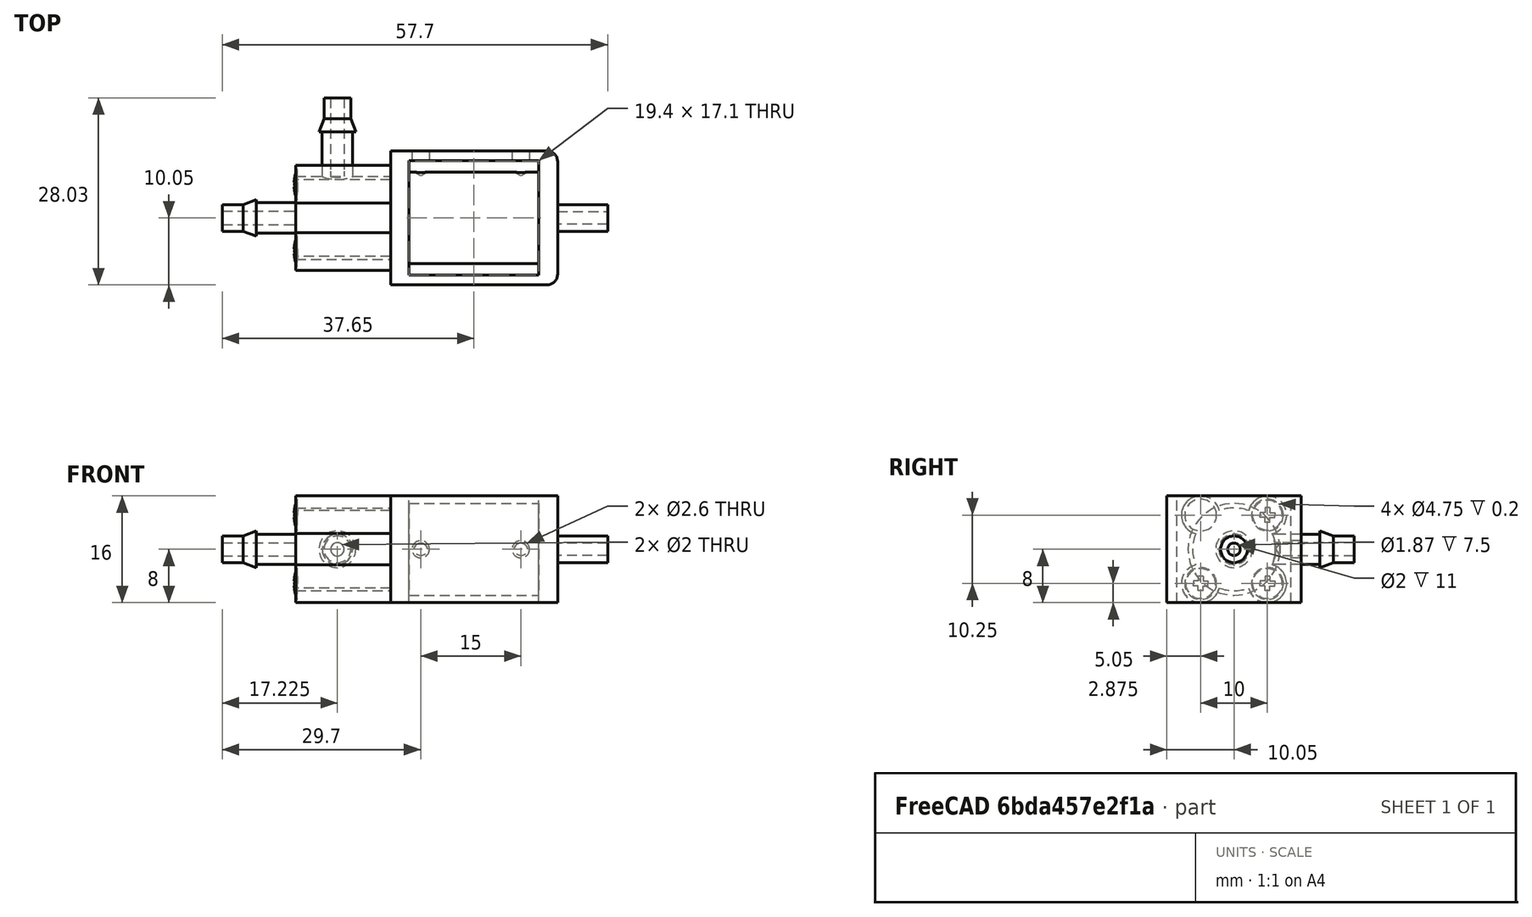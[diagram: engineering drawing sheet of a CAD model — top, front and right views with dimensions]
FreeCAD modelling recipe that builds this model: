
FCSTD DOCUMENT  (FreeCAD 0.19R)
Label: OTS-0004_three-way-valve
License: All rights reserved
LicenseURL: http://en.wikipedia.org/wiki/All_rights_reserved
objects: Sketcher::SketchObject×10, PartDesign::Plane×8, PartDesign::Pad×5, PartDesign::Line×3, PartDesign::Revolution×2, PartDesign::Hole×2, PartDesign::PolarPattern×2, PartDesign::LinearPattern×2, PartDesign::Body×1, PartDesign::FeatureBase×1, PartDesign::Pocket×1
note: 47 computed .brp shape members not serialized (recipe doc carries the construction recipe); baked Part::Feature solids carry a one-line shape summary decoded from their .brp

FEATURE [Sketcher::SketchObject] Sketch
  FullyConstrained = true
  MapMode = 5
  Support = -> [XY_Plane]
  sketch-geometry (14):
    g0: LineSegment StartX=0 StartY=0 StartZ=0 EndX=23.4 EndY=0 EndZ=0
    g1: LineSegment StartX=25 StartY=1.6 StartZ=0 EndX=25 EndY=18.5 EndZ=0
    g2: LineSegment StartX=23.4 StartY=20.1 StartZ=0 EndX=0 EndY=20.1 EndZ=0
    g3: LineSegment StartX=0 StartY=20.1 StartZ=0 EndX=0 EndY=0 EndZ=0
    g4: ArcOfCircle CenterX=23.4 CenterY=18.5 CenterZ=0 NormalX=0 NormalY=0 NormalZ=1 AngleXU=0 Radius=1.6 StartAngle=-9e-16 EndAngle=1.5708
    g5: GeomPoint X=25 Y=20.1 Z=0
    g6: ArcOfCircle CenterX=23.4 CenterY=1.6 CenterZ=0 NormalX=0 NormalY=0 NormalZ=1 AngleXU=0 Radius=1.6 StartAngle=4.71239 EndAngle=6.28319
    g7: GeomPoint X=25 Y=0 Z=0
    g8: LineSegment StartX=2.75 StartY=18.6 StartZ=0 EndX=22.15 EndY=18.6 EndZ=0
    g9: LineSegment StartX=2.75 StartY=18.6 StartZ=0 EndX=2.75 EndY=1.5 EndZ=0
    g10: LineSegment StartX=2.75 StartY=1.5 StartZ=0 EndX=22.15 EndY=1.5 EndZ=0
    g11: GeomPoint X=0 Y=10.05 Z=0
    g12: LineSegment StartX=0 StartY=10.05 StartZ=0 EndX=25 EndY=10.05 EndZ=0
    g13: LineSegment StartX=22.15 StartY=18.6 StartZ=0 EndX=22.15 EndY=1.5 EndZ=0
  constraints (34):
    c: Coincident(g2,g3)
    c: Coincident(g3,g0)
    c: Horizontal(g0)
    c: Horizontal(g2)
    c: Vertical(g1)
    c: Vertical(g3)
    c: Coincident(g0,g-1)
    c: Distance(g0,g7) = 25
    c: Distance(g3) = 20.1
    c: PointOnObject(g5,g1)
    c: PointOnObject(g5,g2)
    c: Tangent(g1,g4) = -1.5708
    c: Tangent(g2,g4) = -1.5708
    c: PointOnObject(g7,g0)
    c: PointOnObject(g7,g1)
    c: Tangent(g0,g6) = -1.5708
    c: Tangent(g1,g6) = -1.5708
    c: Equal(g6,g4)
    c: Diameter(g4) = 3.2
    c: Horizontal(g8)
    c: Coincident(g9,g8)
    c: Vertical(g9)
    c: Coincident(g10,g9)
    c: Horizontal(g10)
    c: Symmetric(g3,g3,g11)
    c: Coincident(g12,g11)
    c: PointOnObject(g12,g1)
    c: Symmetric(g9,g8,g12)
    c: Distance(g9,g3) = 2.75
    c: Coincident(g13,g8)
    c: Coincident(g13,g10)
    c: Vertical(g13)
    c: Distance(g12,g13) = 2.85
    c: Distance(g2,g8) = 1.5
FEATURE [PartDesign::Body] Body  label="3-Way Solenoid Valve"
  BaseFeature = -> DatumPlane001
  Group = -> [BaseFeature,Sketch,Pad,DatumPlane,Sketch001,Pad001,Sketch002,Pad002,Sketch003,Pad003,DatumLine,DatumPlane002,Sketch005,Revolution,DatumPlane003,Sketch007,DatumLine001,PolarPattern,DatumPlane005,Sketch009,Hole001,DatumLine002,DatumPlane006,Sketch010,Revolution001,DatumPlane007,Sketch011,Pocket,LinearPattern,LinearPattern001,Pad004,PolarPattern001,Hole,DatumPlane004,Sketch008]
  Origin = -> Origin
  Tip = -> Pad004
FEATURE [PartDesign::Pad] Pad
  BaseFeature = -> BaseFeature
  Direction = (1,1,1)
  Length = 16
  Length2 = 100
  Midplane = true
  Profile = -> Sketch
  Type = 0
FEATURE [PartDesign::Plane] DatumPlane
  Length = 63.3231
  MapMode = 5
  Placement = pos=(22.15,0,0) rot=(0.57735,-0.57735,-0.57735;2.0944rad)
  ResizeMode = 0
  Support = -> [Pad]
  Width = 60.2981
FEATURE [Sketcher::SketchObject] Sketch001
  ExternalGeometry = -> [Pad]
  FullyConstrained = true
  MapMode = 5
  Placement = pos=(22.15,0,0) rot=(0.57735,-0.57735,-0.57735;2.0944rad)
  Support = -> [DatumPlane]
  sketch-geometry (2):
    g0: Circle CenterX=-10.05 CenterY=-1e-16 CenterZ=0 NormalX=0 NormalY=0 NormalZ=1 AngleXU=0 Radius=6.875
    g1: LineSegment StartX=-18.6 StartY=8 StartZ=0 EndX=-1.5 EndY=-8 EndZ=0
  constraints (4):
    c: Coincident(g1,g-6)
    c: Coincident(g1,g-5)
    c: Symmetric(g1,g1,g0)
    c: Radius(g0) = 6.875
FEATURE [PartDesign::Pad] Pad001
  BaseFeature = -> Pad
  Direction = (1,1,1)
  Length = 10
  Length2 = 100
  Profile = -> Sketch001
  Type = 2
FEATURE [PartDesign::Plane] DatumPlane001
  Length = 63.3231
  MapMode = 5
  Placement = pos=(0,0,0) rot=(0.57735,-0.57735,-0.57735;2.0944rad)
  ResizeMode = 0
  Support = -> [Pad001]
  Width = 60.2981
FEATURE [PartDesign::FeatureBase] BaseFeature
  BaseFeature = -> DatumPlane001
FEATURE [Sketcher::SketchObject] Sketch002
  ExternalGeometry = -> [Pad001]
  FullyConstrained = false
  MapMode = 5
  Placement = pos=(0,0,0) rot=(0.57735,-0.57735,-0.57735;2.0944rad)
  Support = -> [DatumPlane001]
  sketch-geometry (15):
    g0: GeomPoint X=-10.05 Y=1e-16 Z=0
    g1: LineSegment StartX=0 StartY=8 StartZ=0 EndX=-20.1 EndY=-8 EndZ=0
    g2: ArcOfCircle CenterX=-10.05 CenterY=1e-16 CenterZ=0 NormalX=0 NormalY=0 NormalZ=1 AngleXU=0 Radius=6.2 StartAngle=2.75344 EndAngle=3.52974
    g3: ArcOfCircle CenterX=-15.05 CenterY=5.125 CenterZ=0 NormalX=0 NormalY=0 NormalZ=1 AngleXU=0 Radius=2.875 StartAngle=0.235196 EndAngle=4.4525
    g4: ArcOfCircle CenterX=-5.05 CenterY=5.125 CenterZ=0 NormalX=0 NormalY=0 NormalZ=1 AngleXU=0 Radius=2.875 StartAngle=4.97228 EndAngle=9.18958
    g5: LineSegment StartX=-10.05 StartY=1e-16 StartZ=0 EndX=-10.05 EndY=8 EndZ=0
    g6: Circle CenterX=-15.05 CenterY=5.125 CenterZ=0 NormalX=0 NormalY=0 NormalZ=1 AngleXU=0 Radius=2.375
    g7: Circle CenterX=-5.05 CenterY=5.125 CenterZ=0 NormalX=0 NormalY=0 NormalZ=1 AngleXU=0 Radius=2.375
    g8: ArcOfCircle CenterX=-10.05 CenterY=1e-16 CenterZ=0 NormalX=0 NormalY=0 NormalZ=1 AngleXU=0 Radius=6.2 StartAngle=1.20734 EndAngle=1.93425
    g9: ArcOfCircle CenterX=-15.05 CenterY=-5.125 CenterZ=0 NormalX=0 NormalY=0 NormalZ=1 AngleXU=0 Radius=2.875 StartAngle=1.83068 EndAngle=6.04799
    g10: Circle CenterX=-15.05 CenterY=-5.125 CenterZ=0 NormalX=0 NormalY=0 NormalZ=1 AngleXU=0 Radius=2.375
    g11: ArcOfCircle CenterX=-5.05 CenterY=-5.125 CenterZ=0 NormalX=0 NormalY=0 NormalZ=1 AngleXU=0 Radius=2.875 StartAngle=3.37679 EndAngle=7.5941
    g12: Circle CenterX=-5.05 CenterY=-5.125 CenterZ=0 NormalX=0 NormalY=0 NormalZ=1 AngleXU=0 Radius=2.375
    g13: ArcOfCircle CenterX=-10.05 CenterY=1e-16 CenterZ=0 NormalX=0 NormalY=0 NormalZ=1 AngleXU=0 Radius=6.2 StartAngle=4.34893 EndAngle=5.07585
    g14: ArcOfCircle CenterX=-10.05 CenterY=1e-16 CenterZ=0 NormalX=0 NormalY=0 NormalZ=1 AngleXU=0 Radius=6.2 StartAngle=5.89504 EndAngle=6.67133
  constraints (38):
    c: Coincident(g1,g-5)
    c: Coincident(g1,g-4)
    c: Symmetric(g1,g1,g0)
    c: Coincident(g2,g0)
    c: Radius(g2) = 6.2
    c: Tangent(g3,g-5)
    c: Tangent(g4,g-5)
    c: Equal(g3,g4)
    c: Diameter(g3) = 5.75
    c: Distance(g3,g4) = 10
    c: Coincident(g5,g2)
    c: PointOnObject(g5,g-5)
    c: Symmetric(g4,g3,g5)
    c: Coincident(g6,g3)
    c: Coincident(g7,g4)
    c: Equal(g7,g6)
    c: Diameter(g6) = 4.75
    c: Equal(g2,g8)
    c: Coincident(g2,g8)
    c: Coincident(g3,g8)
    c: Coincident(g3,g2)
    c: Coincident(g4,g8)
    c: Coincident(g4,g14)
    c: Equal(g9,g11)
    c: Diameter(g9) = 5.75
    c: Distance(g9,g11) = 10
    c: Coincident(g10,g9)
    c: Coincident(g12,g11)
    c: Equal(g12,g10)
    c: Diameter(g10) = 4.75
    c: Equal(g2,g13)
    c: PointOnObject(g2,g9)
    c: Coincident(g2,g13)
    c: PointOnObject(g13,g9)
    c: Equal(g13,g14)
    c: PointOnObject(g13,g11)
    c: Coincident(g13,g14)
    c: PointOnObject(g14,g11)
FEATURE [PartDesign::Pad] Pad002
  BaseFeature = -> Pad001
  Direction = (1,1,1)
  Length = 14.2
  Length2 = 100
  Profile = -> Sketch002
  Type = 0
FEATURE [Sketcher::SketchObject] Sketch003
  ExternalGeometry = -> [Pad001]
  FullyConstrained = false
  MapMode = 5
  Placement = pos=(0,0,0) rot=(0.57735,-0.57735,-0.57735;2.0944rad)
  Support = -> [DatumPlane001]
  expr: Constraints[25] = Sketch002.Constraints[25]
  expr: Constraints[24] = Sketch002.Constraints[24]
  expr: Constraints[9] = Sketch002.Constraints[9]
  expr: Constraints[16] = Sketch002.Constraints[16]
  expr: Constraints[8] = Sketch002.Constraints[8]
  expr: Constraints[29] = Sketch002.Constraints[29]
  expr: Constraints[4] = Sketch002.Constraints[4]
  sketch-geometry (15):
    g0: GeomPoint X=-10.05 Y=1e-16 Z=0
    g1: LineSegment StartX=0 StartY=8 StartZ=0 EndX=-20.1 EndY=-8 EndZ=0
    g2: ArcOfCircle CenterX=-10.05 CenterY=1e-16 CenterZ=0 NormalX=0 NormalY=0 NormalZ=1 AngleXU=0 Radius=6.2 StartAngle=2.75344 EndAngle=3.52974
    g3: ArcOfCircle CenterX=-15.05 CenterY=5.125 CenterZ=0 NormalX=0 NormalY=0 NormalZ=1 AngleXU=0 Radius=2.875 StartAngle=0.235196 EndAngle=4.4525
    g4: ArcOfCircle CenterX=-5.05 CenterY=5.125 CenterZ=0 NormalX=0 NormalY=0 NormalZ=1 AngleXU=0 Radius=2.875 StartAngle=4.97228 EndAngle=9.18958
    g5: LineSegment StartX=-10.05 StartY=1e-16 StartZ=0 EndX=-10.05 EndY=8 EndZ=0
    g6: Circle CenterX=-15.05 CenterY=5.125 CenterZ=0 NormalX=0 NormalY=0 NormalZ=1 AngleXU=0 Radius=2.375
    g7: Circle CenterX=-5.05 CenterY=5.125 CenterZ=0 NormalX=0 NormalY=0 NormalZ=1 AngleXU=0 Radius=2.375
    g8: ArcOfCircle CenterX=-10.05 CenterY=1e-16 CenterZ=0 NormalX=0 NormalY=0 NormalZ=1 AngleXU=0 Radius=6.2 StartAngle=1.20734 EndAngle=1.93425
    g9: ArcOfCircle CenterX=-15.05 CenterY=-5.125 CenterZ=0 NormalX=0 NormalY=0 NormalZ=1 AngleXU=0 Radius=2.875 StartAngle=1.83068 EndAngle=6.04799
    g10: Circle CenterX=-15.05 CenterY=-5.125 CenterZ=0 NormalX=0 NormalY=0 NormalZ=1 AngleXU=0 Radius=2.375
    g11: ArcOfCircle CenterX=-5.05 CenterY=-5.125 CenterZ=0 NormalX=0 NormalY=0 NormalZ=1 AngleXU=0 Radius=2.875 StartAngle=3.37679 EndAngle=7.5941
    g12: Circle CenterX=-5.05 CenterY=-5.125 CenterZ=0 NormalX=0 NormalY=0 NormalZ=1 AngleXU=0 Radius=2.375
    g13: ArcOfCircle CenterX=-10.05 CenterY=1e-16 CenterZ=0 NormalX=0 NormalY=0 NormalZ=1 AngleXU=0 Radius=6.2 StartAngle=4.34893 EndAngle=5.07585
    g14: ArcOfCircle CenterX=-10.05 CenterY=1e-16 CenterZ=0 NormalX=0 NormalY=0 NormalZ=1 AngleXU=0 Radius=6.2 StartAngle=5.89504 EndAngle=6.67133
  constraints (38):
    c: Coincident(g1,g-5)
    c: Coincident(g1,g-4)
    c: Symmetric(g1,g1,g0)
    c: Coincident(g2,g0)
    c: Radius(g2) = 6.2
    c: Tangent(g3,g-5)
    c: Tangent(g4,g-5)
    c: Equal(g3,g4)
    c: Diameter(g3) = 5.75
    c: Distance(g3,g4) = 10
    c: Coincident(g5,g2)
    c: PointOnObject(g5,g-5)
    c: Symmetric(g4,g3,g5)
    c: Coincident(g6,g3)
    c: Coincident(g7,g4)
    c: Equal(g7,g6)
    c: Diameter(g6) = 4.75
    c: Equal(g2,g8)
    c: Coincident(g2,g8)
    c: Coincident(g3,g8)
    c: Coincident(g3,g2)
    c: Coincident(g4,g8)
    c: Coincident(g4,g14)
    c: Equal(g9,g11)
    c: Diameter(g9) = 5.75
    c: Distance(g9,g11) = 10
    c: Coincident(g10,g9)
    c: Coincident(g12,g11)
    c: Equal(g12,g10)
    c: Diameter(g10) = 4.75
    c: Equal(g2,g13)
    c: PointOnObject(g2,g9)
    c: Coincident(g2,g13)
    c: PointOnObject(g13,g9)
    c: Equal(g13,g14)
    c: PointOnObject(g13,g11)
    c: Coincident(g13,g14)
    c: PointOnObject(g14,g11)
FEATURE [PartDesign::Pad] Pad003
  BaseFeature = -> Pad002
  Direction = (1,1,1)
  Length = 14
  Length2 = 100
  Profile = -> Sketch003
  Type = 0
FEATURE [PartDesign::Line] DatumLine
  AttacherType = Attacher::AttachEngineLine
  Length = 20
  MapMode = 42
  Placement = pos=(0,10.05,5.9e-15) rot=(0.57735,0.57735,0.57735;2.0944rad)
  ResizeMode = 0
  Support = -> [Pad003]
FEATURE [PartDesign::Plane] DatumPlane002
  Length = 64.0876
  MapMode = 3
  Placement = pos=(0,10.05,5.9e-15) rot=(0.707107,0.707107,0;3.14159rad)
  ResizeMode = 0
  Support = -> [DatumLine]
  Width = 68.7626
FEATURE [Sketcher::SketchObject] Sketch005
  FullyConstrained = false
  MapMode = 5
  Placement = pos=(0,10.05,-5e-15) rot=(0.707107,0.707107,0;3.14159rad)
  Support = -> [DatumPlane002]
  sketch-geometry (12):
    g0: LineSegment StartX=0 StartY=-14.2 StartZ=0 EndX=0 EndY=-25.2 EndZ=0
    g1: LineSegment StartX=-2.75 StartY=-20.1 StartZ=0 EndX=-2 EndY=-22.1 EndZ=0
    g2: LineSegment StartX=-2 StartY=-22.1 StartZ=0 EndX=-2 EndY=-25.2 EndZ=0
    g3: LineSegment StartX=-2.75 StartY=-20.1 StartZ=0 EndX=-2.275 EndY=-20.1 EndZ=0
    g4: LineSegment StartX=-2.275 StartY=-20.1 StartZ=0 EndX=-2.275 EndY=-14.2 EndZ=0
    g5: LineSegment StartX=-2.275 StartY=-14.2 StartZ=0 EndX=-1 EndY=-14.1999 EndZ=0
    g6: LineSegment StartX=-2 StartY=-25.2 StartZ=0 EndX=0 EndY=-25.2 EndZ=0
    g7: LineSegment StartX=-2 StartY=-25.2 StartZ=0 EndX=-1 EndY=-25.2 EndZ=0
    g8: LineSegment StartX=-1 StartY=-25.2 StartZ=0 EndX=-1 EndY=-14.1999 EndZ=0
    g9: LineSegment StartX=-2.275 StartY=-14.2 StartZ=0 EndX=-2.275 EndY=-10.8366 EndZ=0
    g10: LineSegment StartX=-2.275 StartY=-10.8366 StartZ=0 EndX=-1 EndY=-10.8366 EndZ=0
    g11: LineSegment StartX=-1 StartY=-14.1999 StartZ=0 EndX=-1 EndY=-10.8366 EndZ=0
  constraints (33):
    c: PointOnObject(g0,g-2)
    c: PointOnObject(g0,g-2)
    c: DistanceY(g-1,g0) = -14.2
    c: Coincident(g2,g1)
    c: Vertical(g2)
    c: Coincident(g3,g1)
    c: Horizontal(g3)
    c: Coincident(g4,g3)
    c: Vertical(g4)
    c: Horizontal(g0,g4)
    c: Coincident(g5,g4)
    c: Coincident(g6,g2)
    c: Coincident(g6,g0)
    c: Horizontal(g6)
    c: Distance(g3,g0) = 2.275
    c: Distance(g4,g3) = 5.9
    c: DistanceX(g6,g6) = 2
    c: Distance(g0) = 11
    c: Distance(g1,g3) = 2
    c: Distance(g1,g0) = 2.75
    c: Coincident(g7,g2)
    c: PointOnObject(g7,g6)
    c: Coincident(g8,g7)
    c: Vertical(g8)
    c: Coincident(g5,g8)
    c: Distance(g7,g0) = 1
    c: Coincident(g9,g4)
    c: Vertical(g9)
    c: Coincident(g10,g9)
    c: Horizontal(g10)
    c: Coincident(g11,g5)
    c: Vertical(g11)
    c: Coincident(g10,g11)
FEATURE [PartDesign::Revolution] Revolution
  Angle = 360
  Axis = (1,-2e-16,-1e-15)
  Base = (0,10.05,-5e-15)
  BaseFeature = -> Pad003
  Profile = -> Sketch005
  ReferenceAxis = -> Sketch005 [V_Axis]
FEATURE [PartDesign::Plane] DatumPlane003
  Length = 68.4424
  MapMode = 5
  Placement = pos=(0,0,0) rot=(1,0,0;1.5708rad)
  ResizeMode = 0
  Support = -> [Revolution]
  Width = 60.7424
FEATURE [Sketcher::SketchObject] Sketch007
  ExternalGeometry = -> [Revolution]
  FullyConstrained = false
  MapMode = 5
  Placement = pos=(0,0,0) rot=(1,0,0;1.5708rad)
  Support = -> [DatumPlane003]
  sketch-geometry (7):
    g0: Circle CenterX=20 CenterY=5 CenterZ=0 NormalX=0 NormalY=0 NormalZ=1 AngleXU=0 Radius=1.2
    g1: Circle CenterX=5 CenterY=-5 CenterZ=0 NormalX=0 NormalY=0 NormalZ=1 AngleXU=0 Radius=1.2
    g2: LineSegment StartX=25 StartY=3.9e-15 StartZ=0 EndX=-25 EndY=3.9e-15 EndZ=0
    g3: LineSegment StartX=20 StartY=5 StartZ=0 EndX=5 EndY=-5 EndZ=0
    g4: GeomPoint X=12.5 Y=0 Z=0
    g5: GeomPoint X=12.5 Y=0 Z=0
    g6: GeomPoint X=-12.918 Y=17.364 Z=0
  constraints (13):
    c: Equal(g0,g1)
    c: Diameter(g0) = 2.4
    c: DistanceY(g0,g1) = -10
    c: DistanceX(g0,g1) = -15
    c: Horizontal(g2)
    c: Symmetric(g-3,g-3,g2)
    c: Symmetric(g0,g1,g2)
    c: Coincident(g3,g0)
    c: Coincident(g3,g1)
    c: Coincident(g5,g4)
    c: Symmetric(g3,g3,g5)
    c: PointOnObject(g4,g-1)
    c: Distance(g0,g-3) = 5
FEATURE [PartDesign::Hole] Hole
  BaseFeature = -> PolarPattern001
  Depth = 3
  DepthType = 0
  Diameter = 2.05
  DrillForDepth = false
  DrillPoint = 1
  DrillPointAngle = 118
  HoleCutCountersinkAngle = 90
  HoleCutCustomValues = false
  HoleCutDepth = 0
  HoleCutDiameter = 6.1
  HoleCutType = 0
  ModelActualThread = false
  Profile = -> Sketch007
  Tapered = false
  TaperedAngle = 90
  ThreadAngle = 60
  ThreadClass = 0
  ThreadCutOffInner = 0.0487139
  ThreadCutOffOuter = 0.0974279
  ThreadDirection = 0
  ThreadFit = 0
  ThreadPitch = 0.45
  ThreadSize = 8
  ThreadType = 1
  Threaded = true
FEATURE [PartDesign::Plane] DatumPlane004
  Length = 63.3231
  MapMode = 5
  Placement = pos=(25,0,0) rot=(0.57735,0.57735,0.57735;2.0944rad)
  ResizeMode = 0
  Support = -> [Hole]
  Width = 60.2981
FEATURE [Sketcher::SketchObject] Sketch008
  ExternalGeometry = -> [Hole]
  FullyConstrained = true
  MapMode = 5
  Placement = pos=(25,0,0) rot=(0.57735,0.57735,0.57735;2.0944rad)
  Support = -> [DatumPlane004]
  sketch-geometry (4):
    g0: Circle CenterX=10.05 CenterY=0 CenterZ=0 NormalX=0 NormalY=0 NormalZ=1 AngleXU=0 Radius=2
    g1: LineSegment StartX=0 StartY=0 StartZ=0 EndX=10.05 EndY=0 EndZ=0
    g2: LineSegment StartX=10.05 StartY=0 StartZ=0 EndX=20.1 EndY=0 EndZ=0
    g3: Circle CenterX=10.05 CenterY=0 CenterZ=0 NormalX=0 NormalY=0 NormalZ=1 AngleXU=0 Radius=0.935
  constraints (10):
    c: PointOnObject(g0,g-1)
    c: Diameter(g0) = 4
    c: Coincident(g1,g-1)
    c: Coincident(g1,g0)
    c: Coincident(g2,g0)
    c: Equal(g1,g2)
    c: Coincident(g3,g0)
    c: Diameter(g3) = 1.87
    c: Horizontal(g2)
    c: DistanceX(g-2,g2) = 10.05
FEATURE [PartDesign::Line] DatumLine001
  AttacherType = Attacher::AttachEngineLine
  AttachmentOffset = pos=(6.6,0.375,0) rot=(0,0,1;0rad)
  Length = 20
  MapMode = 44
  Placement = pos=(-7.6,10.425,5.72e-14) rot=(0,0,1;0rad)
  ResizeMode = 0
  Support = -> [Revolution]
FEATURE [PartDesign::PolarPattern] PolarPattern
  Angle = 90
  Axis = -> DatumLine001
  BaseFeature = -> Revolution
  Occurrences = 2
  Originals = -> [Revolution]
  Reversed = true
FEATURE [PartDesign::Plane] DatumPlane005
  Length = 68.4424
  MapMode = 5
  Placement = pos=(0,20.1,0) rot=(0,0.707107,0.707107;3.14159rad)
  ResizeMode = 0
  Support = -> [PolarPattern]
  Width = 60.7424
FEATURE [Sketcher::SketchObject] Sketch009
  FullyConstrained = false
  MapMode = 5
  Placement = pos=(0,20.1,0) rot=(0,0.707107,0.707107;3.14159rad)
  Support = -> [DatumPlane005]
  sketch-geometry (2):
    g0: Circle CenterX=-19.5 CenterY=0 CenterZ=0 NormalX=0 NormalY=0 NormalZ=1 AngleXU=0 Radius=1.3
    g1: Circle CenterX=-4.5 CenterY=0 CenterZ=0 NormalX=0 NormalY=0 NormalZ=1 AngleXU=0 Radius=1.3
  constraints (5):
    c: PointOnObject(g0,g-1)
    c: PointOnObject(g1,g-1)
    c: Equal(g0,g1)
    c: DistanceX(g0,g1) = 15
    c: Radius(g0) = 1.3
FEATURE [PartDesign::Hole] Hole001
  BaseFeature = -> PolarPattern
  Depth = 3
  DepthType = 0
  Diameter = 2.6
  DrillForDepth = false
  DrillPoint = 1
  DrillPointAngle = 118
  HoleCutCountersinkAngle = 90
  HoleCutCustomValues = false
  HoleCutDepth = 0
  HoleCutDiameter = 6.1
  HoleCutType = 0
  ModelActualThread = false
  Profile = -> Sketch009
  Tapered = false
  TaperedAngle = 90
  ThreadAngle = 0
  ThreadClass = 0
  ThreadCutOffInner = 0
  ThreadCutOffOuter = 0
  ThreadDirection = 0
  ThreadFit = 1
  ThreadPitch = 0
  ThreadSize = 0
  ThreadType = 0
  Threaded = false
FEATURE [PartDesign::Line] DatumLine002
  AttacherType = Attacher::AttachEngineLine
  Length = 20
  MapMode = 42
  Placement = pos=(2.043e-13,15.05,-5.125) rot=(0.57735,0.57735,0.57735;2.0944rad)
  ResizeMode = 0
  Support = -> [Hole001]
FEATURE [PartDesign::Plane] DatumPlane006
  Length = 64.0876
  MapMode = 3
  Placement = pos=(2.043e-13,15.05,-5.125) rot=(0.707107,0.707107,0;3.14159rad)
  ResizeMode = 0
  Support = -> [DatumLine002]
  Width = 68.7626
FEATURE [Sketcher::SketchObject] Sketch010
  FullyConstrained = false
  MapMode = 5
  Placement = pos=(2.043e-13,15.05,-5.125) rot=(0.707107,0.707107,0;3.14159rad)
  Support = -> [DatumPlane006]
  sketch-geometry (5):
    g0: LineSegment StartX=0 StartY=-13.9894 StartZ=0 EndX=2.2332 EndY=-13.9894 EndZ=0
    g1: LineSegment StartX=2.2332 StartY=-13.9894 StartZ=0 EndX=2.2332 EndY=-14.0417 EndZ=0
    g2: LineSegment StartX=0 StartY=-13.9894 StartZ=0 EndX=0 EndY=-14.481 EndZ=0
    g3: ArcOfCircle CenterX=-7.65987e-08 CenterY=-8.58399 CenterZ=0 NormalX=0 NormalY=0 NormalZ=1 AngleXU=0 Radius=5.89698 StartAngle=4.71239 EndAngle=5.10078
    g4: LineSegment StartX=0 StartY=-14.481 StartZ=0 EndX=1.96099 EndY=-14.481 EndZ=0
  constraints (11):
    c: PointOnObject(g0,g-2)
    c: Horizontal(g0)
    c: Coincident(g1,g0)
    c: Vertical(g1)
    c: Coincident(g2,g0)
    c: PointOnObject(g2,g-2)
    c: Coincident(g3,g1)
    c: Coincident(g3,g2)
    c: Coincident(g4,g2)
    c: Horizontal(g4)
    c: Tangent(g4,g3)
FEATURE [PartDesign::Revolution] Revolution001
  Angle = 360
  Axis = (1,-1.34e-14,-1e-16)
  Base = (2.043e-13,15.05,-5.125)
  BaseFeature = -> Hole001
  Profile = -> Sketch010
  ReferenceAxis = -> DatumLine002
FEATURE [PartDesign::Plane] DatumPlane007
  Length = 63.3231
  MapMode = 45
  Placement = pos=(-14.2614,15.05,-5.125) rot=(0.57735,0.57735,0.57735;2.0944rad)
  ResizeMode = 0
  Support = -> [Revolution001]
  Width = 60.2981
FEATURE [Sketcher::SketchObject] Sketch011
  FullyConstrained = true
  MapMode = 5
  Placement = pos=(-14.2614,15.05,-5.125) rot=(0.57735,0.57735,0.57735;2.0944rad)
  Support = -> [DatumPlane007]
  sketch-geometry (17):
    g0: LineSegment StartX=0.366667 StartY=1.1 StartZ=0 EndX=-0.366667 EndY=1.1 EndZ=0
    g1: LineSegment StartX=-0.366667 StartY=1.1 StartZ=0 EndX=-0.366667 EndY=0.366667 EndZ=0
    g2: LineSegment StartX=-0.366667 StartY=0.366667 StartZ=0 EndX=-1.1 EndY=0.366667 EndZ=0
    g3: LineSegment StartX=-1.1 StartY=0.366667 StartZ=0 EndX=-1.1 EndY=0 EndZ=0
    g4: LineSegment StartX=0.366667 StartY=1.1 StartZ=0 EndX=0.366667 EndY=0.366667 EndZ=0
    g5: LineSegment StartX=0.366667 StartY=0.366667 StartZ=0 EndX=1.1 EndY=0.366667 EndZ=0
    g6: LineSegment StartX=1.1 StartY=0.366667 StartZ=0 EndX=1.1 EndY=0 EndZ=0
    g7: LineSegment StartX=-0.366667 StartY=0.366667 StartZ=0 EndX=0.366667 EndY=0.366667 EndZ=0
    g8: LineSegment StartX=0.366667 StartY=-1.1 StartZ=0 EndX=-0.366667 EndY=-1.1 EndZ=0
    g9: LineSegment StartX=-0.366667 StartY=-1.1 StartZ=0 EndX=-0.366667 EndY=-0.366667 EndZ=0
    g10: LineSegment StartX=-0.366667 StartY=-0.366667 StartZ=0 EndX=-1.1 EndY=-0.366667 EndZ=0
    g11: LineSegment StartX=-1.1 StartY=-0.366667 StartZ=0 EndX=-1.1 EndY=0 EndZ=0
    g12: LineSegment StartX=0.366667 StartY=-1.1 StartZ=0 EndX=0.366667 EndY=-0.366667 EndZ=0
    g13: LineSegment StartX=0.366667 StartY=-0.366667 StartZ=0 EndX=1.1 EndY=-0.366667 EndZ=0
    g14: LineSegment StartX=1.1 StartY=-0.366667 StartZ=0 EndX=1.1 EndY=0 EndZ=0
    g15: LineSegment StartX=-0.366667 StartY=-0.366667 StartZ=0 EndX=0.366667 EndY=-0.366667 EndZ=0
    g16: LineSegment StartX=-0.366667 StartY=-0.366667 StartZ=0 EndX=-0.366667 EndY=0.366667 EndZ=0
  constraints (47):
    c: Vertical(g1)
    c: Coincident(g2,g1)
    c: Horizontal(g2)
    c: Coincident(g3,g2)
    c: Vertical(g3)
    c: Vertical(g4)
    c: Horizontal(g5)
    c: PointOnObject(g6,g-1)
    c: Vertical(g6)
    c: PointOnObject(g3,g-1)
    c: Equal(g5,g2)
    c: Coincident(g6,g5)
    c: Equal(g6,g3)
    c: Coincident(g4,g5)
    c: Coincident(g0,g4)
    c: Coincident(g0,g1)
    c: Symmetric(g0,g0,g-2)
    c: Equal(g1,g2)
    c: Coincident(g7,g1)
    c: Coincident(g7,g4)
    c: Equal(g2,g7)
    c: Vertical(g9)
    c: Coincident(g10,g9)
    c: Horizontal(g10)
    c: Coincident(g11,g10)
    c: Vertical(g11)
    c: Vertical(g12)
    c: Horizontal(g13)
    c: Vertical(g14)
    c: Equal(g13,g10)
    c: Coincident(g14,g13)
    c: Equal(g14,g11)
    c: Coincident(g12,g13)
    c: Coincident(g8,g12)
    c: Coincident(g8,g9)
    c: Equal(g9,g10)
    c: Coincident(g15,g9)
    c: Coincident(g15,g12)
    c: Equal(g10,g15)
    c: Coincident(g3,g11)
    c: Coincident(g6,g14)
    c: Horizontal(g8)
    c: Equal(g11,g3)
    c: Coincident(g16,g9)
    c: Coincident(g16,g1)
    c: Equal(g16,g7)
    c: Distance(g2,g5) = 2.2
FEATURE [PartDesign::Pocket] Pocket
  BaseFeature = -> Revolution001
  Length = 0.625
  Length2 = 100
  Midplane = true
  Profile = -> Sketch011
  Type = 0
FEATURE [PartDesign::PolarPattern] PolarPattern001
  Angle = 180
  Axis = -> DatumLine
  BaseFeature = -> Pad004
  Occurrences = 2
  Originals = -> [Revolution001,Pocket]
FEATURE [PartDesign::LinearPattern] LinearPattern001
  BaseFeature = -> LinearPattern
  Direction = -> Z_Axis
  Length = 10.25
  Occurrences = 2
  Originals = -> [Revolution001,Pocket]
FEATURE [PartDesign::LinearPattern] LinearPattern
  BaseFeature = -> Pocket
  Direction = -> Y_Axis
  Length = 10
  Occurrences = 2
  Originals = -> [Revolution001,Pocket]
  Reversed = true
FEATURE [PartDesign::Pad] Pad004
  BaseFeature = -> LinearPattern001
  Direction = (1,1,1)
  Length = 7.5
  Length2 = 100
  Profile = -> Sketch008
  Type = 0
